MODEL slx_e3e4152165c9
CONFIG AbsTol = auto
CONFIG FixedStep = 0.01
CONFIG MaxStep = auto
CONFIG MinStep = auto
CONFIG RelTol = 1e-3
CONFIG SampleTimeConstraint = Unconstrained
CONFIG Solver = ode5
CONFIG SolverMode = Auto
CONFIG SolverName = ode5
CONFIG StartTime = 0.0
CONFIG StopTime = 10.0
BLOCK [Constant] Constant
  Value = phi_dot
BLOCK [Constant] Constant1
  Value = beta_dot
BLOCK [SubSystem] DKM
  Ports = [2, 3]
  RequestExecContextInheritance = off
BLOCK [Constant] DKM/Constant
  Value = r
BLOCK [Constant] DKM/Constant1
  Value = a
BLOCK [Fcn] DKM/Fcn
  Expr = sin(u)
BLOCK [Fcn] DKM/Fcn1
  Expr = cos(u)
BLOCK [Fcn] DKM/Fcn2
  Expr = sin(u)
BLOCK [Fcn] DKM/Fcn3
  Expr = cos(u)
BLOCK [Integrator] DKM/Integrator
  InitialCondition = beta0
  Ports = [1, 1]
BLOCK [Integrator] DKM/Integrator1
  Ports = [1, 1]
BLOCK [Integrator] DKM/Integrator2
  Ports = [1, 1]
BLOCK [Integrator] DKM/Integrator3
  Ports = [1, 1]
BLOCK [Product] DKM/Product
  InputSameDT = off
  Inputs = **/
  OutDataTypeStr = Inherit: Inherit via internal rule
  Ports = [3, 1]
  RndMeth = Floor
  SaturateOnIntegerOverflow = off
BLOCK [Product] DKM/Product1
  InputSameDT = off
  OutDataTypeStr = Inherit: Inherit via internal rule
  Ports = [2, 1]
  RndMeth = Floor
  SaturateOnIntegerOverflow = off
BLOCK [Product] DKM/Product2
  InputSameDT = off
  Inputs = 4
  OutDataTypeStr = Inherit: Inherit via internal rule
  Ports = [4, 1]
  RndMeth = Floor
  SaturateOnIntegerOverflow = off
BLOCK [Product] DKM/Product3
  InputSameDT = off
  Inputs = 4
  OutDataTypeStr = Inherit: Inherit via internal rule
  Ports = [4, 1]
  RndMeth = Floor
  SaturateOnIntegerOverflow = off
BLOCK [ToWorkspace] DKM/To Workspace
  FixptAsFi = on
  MaxDataPoints = inf
  Ports = [1]
  SampleTime = -1
  Save2DSignal = 3-D array (concatenate along third dimension)
  VariableName = beta
BLOCK [Inport] DKM/beta_dot
  IconDisplay = Port number
  Port = 2
BLOCK [Inport] DKM/phi_dot
  IconDisplay = Port number
BLOCK [Outport] DKM/theta
  IconDisplay = Port number
  Port = 3
BLOCK [Outport] DKM/x
  IconDisplay = Port number
BLOCK [Outport] DKM/y
  IconDisplay = Port number
  Port = 2
BLOCK [Mux] Mux
  DisplayOption = bar
  Inputs = 3
  Ports = [3, 1]
BLOCK [ToWorkspace] To Workspace
  FixptAsFi = on
  MaxDataPoints = inf
  Ports = [1]
  SampleTime = -1
  Save2DSignal = 3-D array (concatenate along third dimension)
  VariableName = p
LINE Constant1:1 -> DKM:2
LINE Constant:1 -> DKM:1
LINE DKM/Constant1:1 -> DKM/Product2:2
LINE DKM/Constant1:1 -> DKM/Product3:2
LINE DKM/Constant1:1 -> DKM/Product:3
LINE DKM/Constant:1 -> DKM/Product:2
LINE DKM/Fcn1:1 -> DKM/Product2:3
LINE DKM/Fcn1:1 -> DKM/Product3:3
LINE DKM/Fcn2:1 -> DKM/Product3:4
LINE DKM/Fcn3:1 -> DKM/Product2:4
LINE DKM/Fcn:1 -> DKM/Product1:2
LINE DKM/Integrator1:1 -> DKM/Fcn2:1
LINE DKM/Integrator1:1 -> DKM/Fcn3:1
LINE DKM/Integrator1:1 -> DKM/theta:1
LINE DKM/Integrator2:1 -> DKM/x:1
LINE DKM/Integrator3:1 -> DKM/y:1
LINE DKM/Integrator:1 -> DKM/Fcn1:1
LINE DKM/Integrator:1 -> DKM/Fcn:1
LINE DKM/Integrator:1 -> DKM/To Workspace:1
LINE DKM/Product1:1 -> DKM/Integrator1:1
LINE DKM/Product2:1 -> DKM/Integrator2:1
LINE DKM/Product3:1 -> DKM/Integrator3:1
LINE DKM/Product:1 -> DKM/Product1:1
LINE DKM/Product:1 -> DKM/Product2:1
LINE DKM/Product:1 -> DKM/Product3:1
LINE DKM/beta_dot:1 -> DKM/Integrator:1
LINE DKM/phi_dot:1 -> DKM/Product:1
LINE DKM:1 -> Mux:1
LINE DKM:2 -> Mux:2
LINE DKM:3 -> Mux:3
LINE Mux:1 -> To Workspace:1
